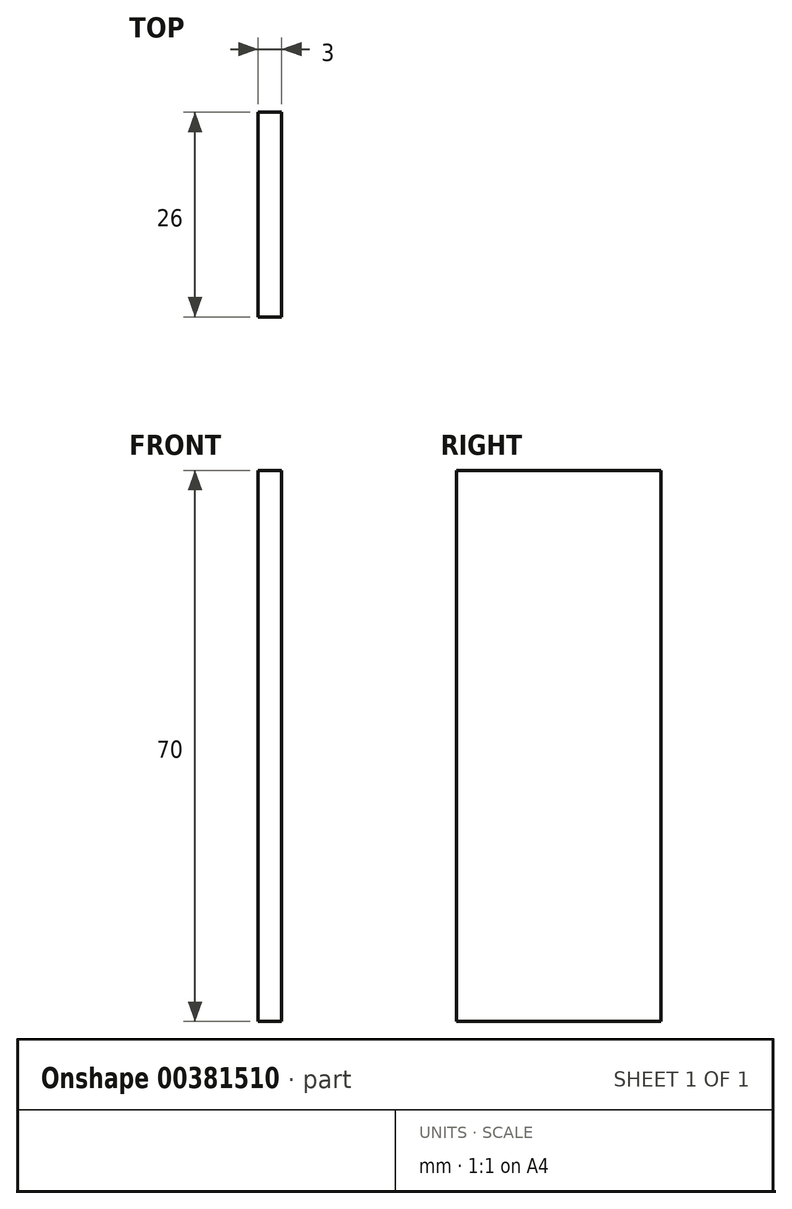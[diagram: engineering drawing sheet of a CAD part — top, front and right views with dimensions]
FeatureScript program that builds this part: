
annotation { "Feature Type Name" : "Feature", "Feature Type Description" : "" }
export const myFeature = defineFeature(function(context is Context, id is Id, definition is map)
    precondition{}
    {
        {
            var Q0;
            Q0=qCreatedBy(makeId("Right.planeOp"),FACE);
            var sketch = newSketch(context, id + "F0", { "sketchPlane" : qUnion([Q0])});
            skLineSegment(sketch, "E0", {"start": v(-5, 27.93) * mm, "end": v(21, 27.93) * mm});
            skLineSegment(sketch, "E1", {"start": v(21, 27.93) * mm, "end": v(21, -42.07) * mm});
            skLineSegment(sketch, "E2", {"start": v(21, -42.07) * mm, "end": v(-5, -42.07) * mm});
            skLineSegment(sketch, "E3", {"start": v(-5, 27.93) * mm, "end": v(-5, -42.07) * mm});
            skSolve(sketch);
        }
        {
            var Q0;
            Q0=makeQuery(id+"F0.imprint","IMPRINT",FACE,{"disambiguationData":[TD([[makeQuery(id+"F0.imprint","IMPRINT",EDGE,{"derivedFrom":sQuery(id+"F0.wireOp",EDGE,"E0")}),-1.0]])]});
            extrude(context, id + "F1", {"entities" : qUnion([Q0]), "endBound" : BoundingType.SYMMETRIC, "depth" : 3 * mm});
        }
    });
